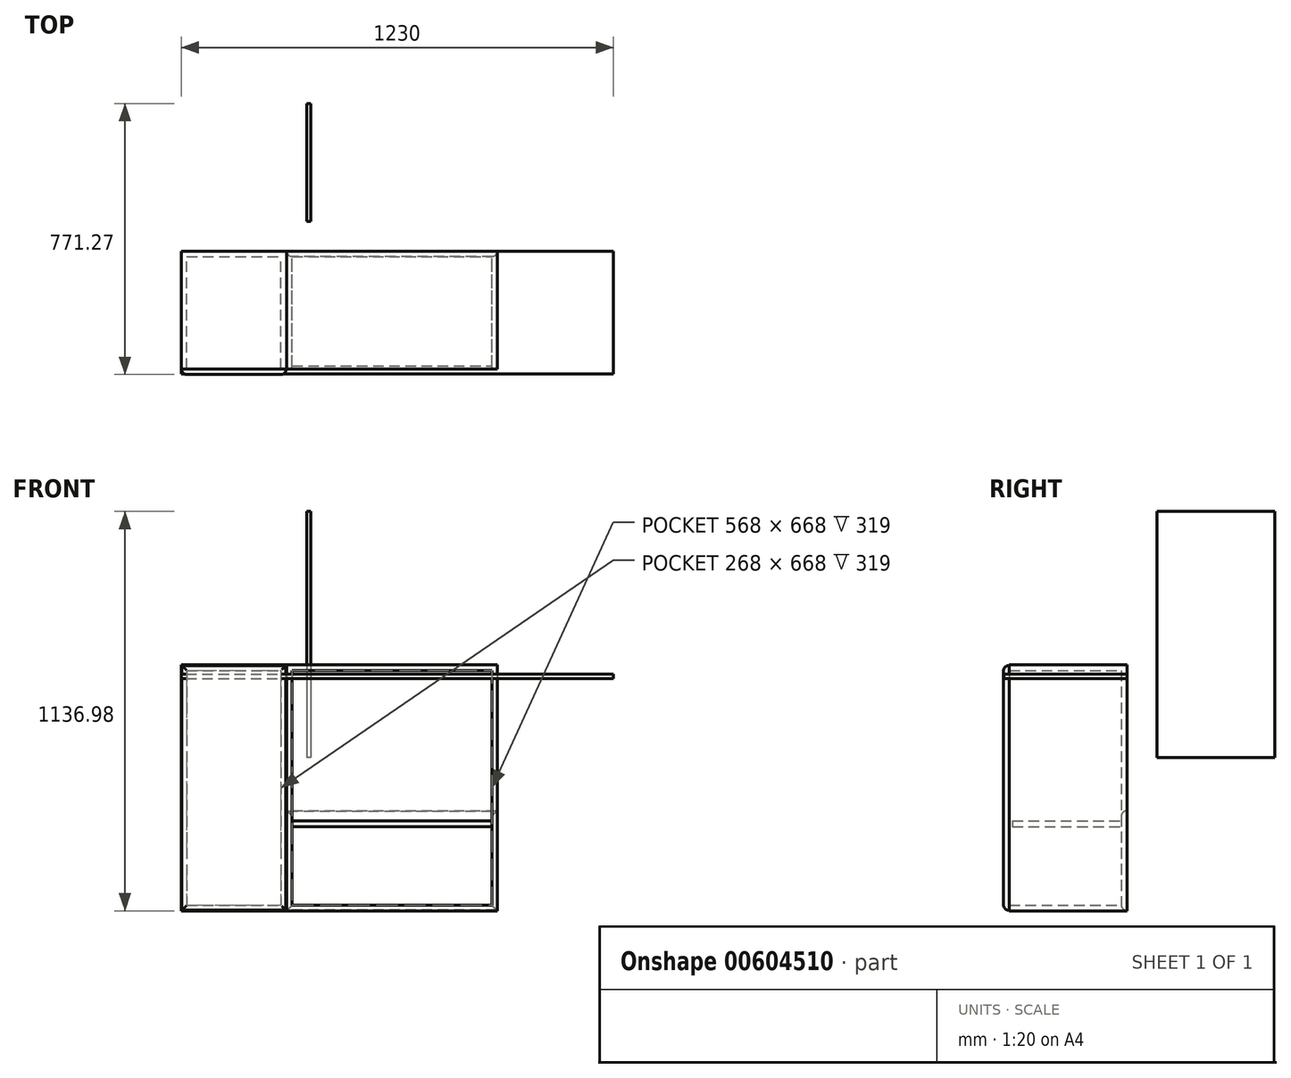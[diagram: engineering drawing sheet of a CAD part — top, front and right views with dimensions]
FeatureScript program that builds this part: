
annotation { "Feature Type Name" : "Feature", "Feature Type Description" : "" }
export const myFeature = defineFeature(function(context is Context, id is Id, definition is map)
    precondition{}
    {
        {
            var Q0;
            Q0=qCreatedBy(makeId("Front.planeOp"),FACE);
            var sketch = newSketch(context, id + "F0", { "sketchPlane" : qUnion([Q0])});
            skLineSegment(sketch, "E0.bottom", {"start": v(-357.2, 38.32) * mm, "end": v(-57.2, 38.32) * mm});
            skLineSegment(sketch, "E0.top", {"start": v(-357.2, -661.68) * mm, "end": v(-57.2, -661.68) * mm});
            skLineSegment(sketch, "E0.left", {"start": v(-357.2, 38.32) * mm, "end": v(-357.2, -661.68) * mm});
            skLineSegment(sketch, "E0.right", {"start": v(-57.2, 38.32) * mm, "end": v(-57.2, -661.68) * mm});
            skSolve(sketch);
        }
        {
            var Q0;
            Q0=qSketchRegion(id+"F0",true);
            extrude(context, id + "F1", {"entities" : qUnion([Q0]), "depth" : 335 * mm});
        }
        {
            var Q0;
            Q0=makeQuery(id+"F1.opExtrude","CAP_FACE",FACE,{"disambiguationData":[OSD([sQuery(id+"F0.wireOp",EDGE,"E0.bottom"),sQuery(id+"F0.wireOp",EDGE,"E0.top"),sQuery(id+"F0.wireOp",EDGE,"E0.left"),sQuery(id+"F0.wireOp",EDGE,"E0.right")])],"isStart":false});
            shell(context, id + "F2", {"entities" : qUnion([Q0]), "thickness" : 16 * mm});
        }
        {
            var Q0;
            Q0=qCreatedBy(makeId("Front.planeOp"),FACE);
            var sketch = newSketch(context, id + "F3", { "sketchPlane" : qUnion([Q0])});
            skLineSegment(sketch, "E1.0", {"start": v(-57.2, 38.32) * mm, "end": v(-57.2, -661.68) * mm});
            skLineSegment(sketch, "E2.bottom", {"start": v(-57.2, 38.32) * mm, "end": v(542.8, 38.32) * mm});
            skLineSegment(sketch, "E2.top", {"start": v(-57.2, -661.68) * mm, "end": v(542.8, -661.68) * mm});
            skLineSegment(sketch, "E2.right", {"start": v(542.8, 38.32) * mm, "end": v(542.8, -661.68) * mm});
            skSolve(sketch);
        }
        {
            var Q0;
            Q0=qSketchRegion(id+"F3",true);
            extrude(context, id + "F4", {"entities" : qUnion([Q0]), "depth" : 335 * mm});
        }
        {
            var Q0;
            Q0=makeQuery(id+"F4.opExtrude","CAP_FACE",FACE,{"disambiguationData":[OSD([sQuery(id+"F3.wireOp",EDGE,"E2.bottom"),sQuery(id+"F3.wireOp",EDGE,"E2.top"),sQuery(id+"F3.wireOp",EDGE,"E1.0"),sQuery(id+"F3.wireOp",EDGE,"E2.right")])],"isStart":false});
            shell(context, id + "F5", {"entities" : qUnion([Q0]), "thickness" : 16 * mm});
        }
        {
            var Q0;
            Q0=makeQuery(id+"F5.opShell","OFFSET_FACE",FACE,{"disambiguationData":[OSD([sQuery(id+"F3.wireOp",EDGE,"E2.bottom"),sQuery(id+"F3.wireOp",EDGE,"E2.top"),sQuery(id+"F3.wireOp",EDGE,"E1.0"),sQuery(id+"F3.wireOp",EDGE,"E2.right")])]});
            var sketch = newSketch(context, id + "F6", { "sketchPlane" : qUnion([Q0])});
            skLineSegment(sketch, "E3.bottom", {"start": v(-41.2, -405.81) * mm, "end": v(526.8, -405.81) * mm});
            skLineSegment(sketch, "E3.top", {"start": v(-41.2, -421.81) * mm, "end": v(526.8, -421.81) * mm});
            skLineSegment(sketch, "E3.left", {"start": v(-41.2, -405.81) * mm, "end": v(-41.2, -421.81) * mm});
            skLineSegment(sketch, "E3.right", {"start": v(526.8, -405.81) * mm, "end": v(526.8, -421.81) * mm});
            skSolve(sketch);
        }
        {
            var Q0;
            Q0=qSketchRegion(id+"F6",true);
            extrude(context, id + "F7", {"entities" : qUnion([Q0]), "depth" : 310 * mm});
        }
        {
            var Q0;
            Q0=makeQuery(id+"F1.opExtrude","CAP_FACE",FACE,{"disambiguationData":[OSD([sQuery(id+"F0.wireOp",EDGE,"E0.bottom"),sQuery(id+"F0.wireOp",EDGE,"E0.top"),sQuery(id+"F0.wireOp",EDGE,"E0.left"),sQuery(id+"F0.wireOp",EDGE,"E0.right")])],"isStart":false});
            var sketch = newSketch(context, id + "F8", { "sketchPlane" : qUnion([Q0])});
            skPoint(sketch, "E4.0", {"position": v(-357.2, 38.32) * mm});
            skPoint(sketch, "E5.0", {"position": v(-57.2, -661.68) * mm});
            skLineSegment(sketch, "E6.bottom", {"start": v(-355.2, 36.32) * mm, "end": v(-59.2, 36.32) * mm});
            skLineSegment(sketch, "E6.top", {"start": v(-355.2, -659.68) * mm, "end": v(-59.2, -659.68) * mm});
            skLineSegment(sketch, "E6.left", {"start": v(-355.2, 36.32) * mm, "end": v(-355.2, -659.68) * mm});
            skLineSegment(sketch, "E6.right", {"start": v(-59.2, 36.32) * mm, "end": v(-59.2, -659.68) * mm});
            skSolve(sketch);
        }
        {
            var Q0;
            Q0=qSketchRegion(id+"F8",true);
            extrude(context, id + "F9", {"entities" : qUnion([Q0]), "depth" : 16 * mm});
        }
        {
            var Q0;
            Q0=qCreatedBy(makeId("Right.planeOp"),FACE);
            var sketch = newSketch(context, id + "F10", { "sketchPlane" : qUnion([Q0])});
            skLineSegment(sketch, "E7.bottom", {"start": v(85.27, 475.3) * mm, "end": v(420.27, 475.3) * mm});
            skLineSegment(sketch, "E7.top", {"start": v(85.27, -224.7) * mm, "end": v(420.27, -224.7) * mm});
            skLineSegment(sketch, "E7.left", {"start": v(85.27, 475.3) * mm, "end": v(85.27, -224.7) * mm});
            skLineSegment(sketch, "E7.right", {"start": v(420.27, 475.3) * mm, "end": v(420.27, -224.7) * mm});
            skSolve(sketch);
        }
        {
            var Q0;
            Q0=qSketchRegion(id+"F10",true);
            extrude(context, id + "F11", {"entities" : qUnion([Q0]), "depth" : 12 * mm});
        }
        {
            var Q0;
            Q0=qCreatedBy(makeId("Top.planeOp"),FACE);
            var sketch = newSketch(context, id + "F12", { "sketchPlane" : qUnion([Q0])});
            skPoint(sketch, "E8.0", {"position": v(-357.2, 0) * mm});
            skLineSegment(sketch, "E9.bottom", {"start": v(-357.2, 0) * mm, "end": v(872.8, 0) * mm});
            skLineSegment(sketch, "E9.top", {"start": v(-357.2, -350) * mm, "end": v(872.8, -350) * mm});
            skLineSegment(sketch, "E9.left", {"start": v(-357.2, 0) * mm, "end": v(-357.2, -350) * mm});
            skLineSegment(sketch, "E9.right", {"start": v(872.8, 0) * mm, "end": v(872.8, -350) * mm});
            skSolve(sketch);
        }
        {
            var Q0;
            Q0=qSketchRegion(id+"F12",true);
            extrude(context, id + "F13", {"entities" : qUnion([Q0]), "depth" : 12 * mm});
        }
        {
            var Q0;
            Q0=makeQuery(id+"F9.opExtrude","CAP_FACE",FACE,{"disambiguationData":[OSD([sQuery(id+"F8.wireOp",EDGE,"E6.bottom"),sQuery(id+"F8.wireOp",EDGE,"E6.top"),sQuery(id+"F8.wireOp",EDGE,"E6.left"),sQuery(id+"F8.wireOp",EDGE,"E6.right")])],"isStart":false});
            fillet(context, id + "F14", {"entities" : qUnion([Q0]), "radius" : 12 * mm, "tangentPropagation" : true, "rho" : 0.3, "crossSection" : FilletCrossSection.CONIC, "allowEdgeOverflow" : false});
        }
        {
            var Q0;
            Q0=qCreatedBy(makeId("Front.planeOp"),FACE);
            var sketch = newSketch(context, id + "F15", { "sketchPlane" : qUnion([Q0])});
            skPoint(sketch, "E10.0", {"position": v(542.8, -661.68) * mm});
            skPoint(sketch, "E11.0", {"position": v(-57.2, -661.68) * mm});
            skLineSegment(sketch, "E12.bottom", {"start": v(540.8, -659.68) * mm, "end": v(-55.2, -659.68) * mm});
            skLineSegment(sketch, "E12.top", {"start": v(540.8, -377.68) * mm, "end": v(-55.2, -377.68) * mm});
            skLineSegment(sketch, "E12.left", {"start": v(540.8, -659.68) * mm, "end": v(540.8, -377.68) * mm});
            skLineSegment(sketch, "E12.right", {"start": v(-55.2, -659.68) * mm, "end": v(-55.2, -377.68) * mm});
            skSolve(sketch);
        }
        {
            var Q0;
            Q0=qSketchRegion(id+"F15",true);
            extrude(context, id + "F16", {"entities" : qUnion([Q0]), "depth" : 16 * mm});
        }
        {
            var Q0;
            Q0=makeQuery(id+"F16.opExtrude","CAP_FACE",FACE,{"disambiguationData":[OSD([sQuery(id+"F15.wireOp",EDGE,"E12.bottom"),sQuery(id+"F15.wireOp",EDGE,"E12.top"),sQuery(id+"F15.wireOp",EDGE,"E12.left"),sQuery(id+"F15.wireOp",EDGE,"E12.right")])],"isStart":false});
            fillet(context, id + "F17", {"entities" : qUnion([Q0]), "radius" : 12 * mm, "tangentPropagation" : true, "rho" : 0.3, "crossSection" : FilletCrossSection.CONIC, "allowEdgeOverflow" : false});
        }
    });
